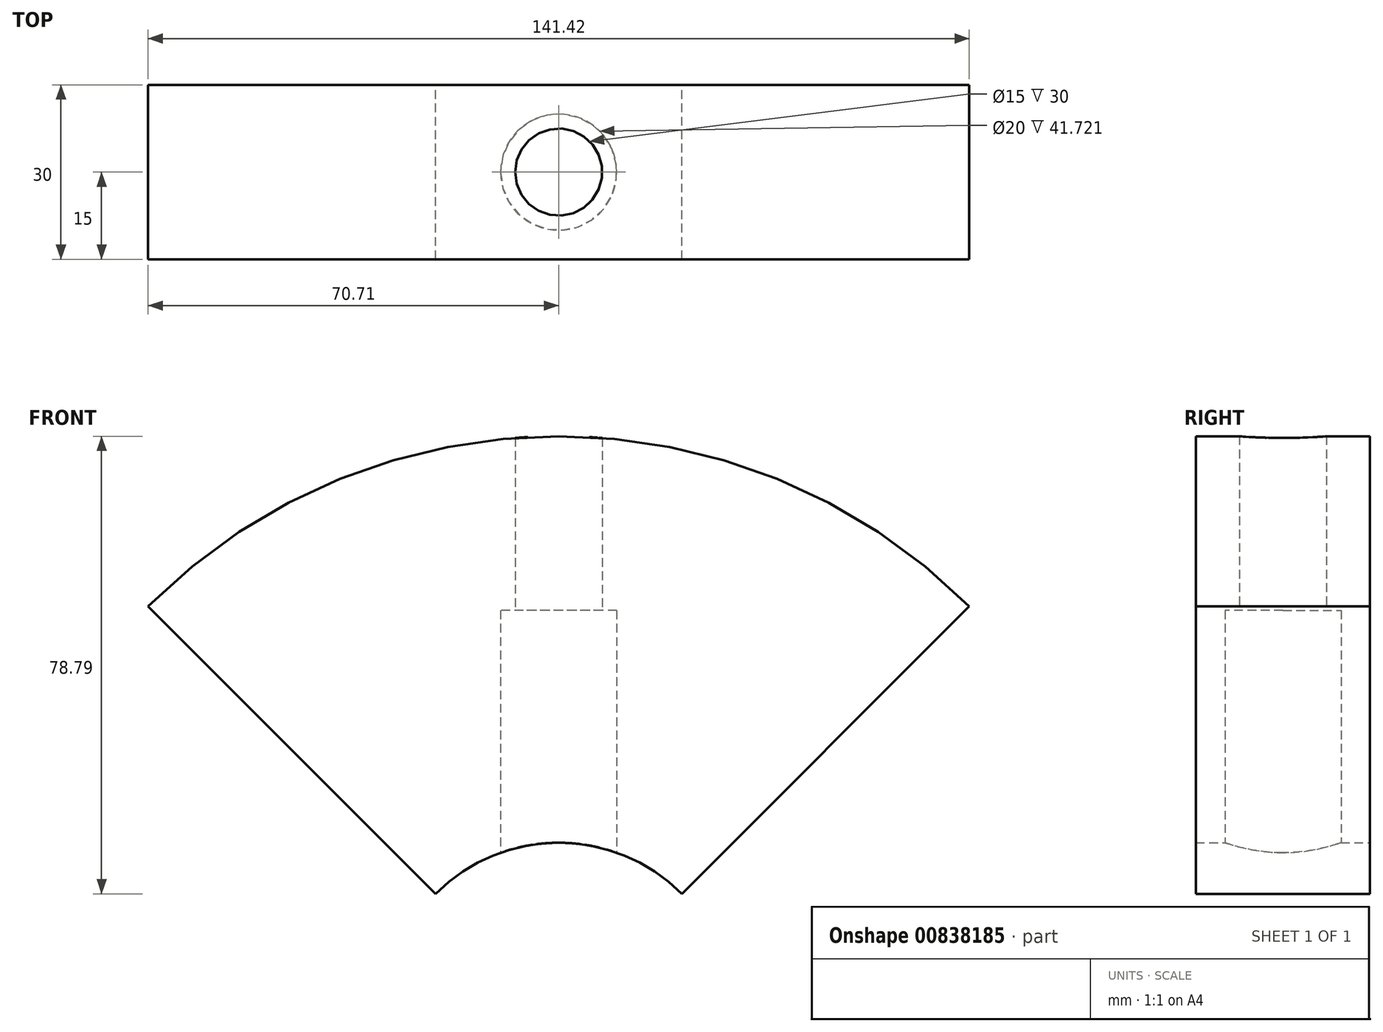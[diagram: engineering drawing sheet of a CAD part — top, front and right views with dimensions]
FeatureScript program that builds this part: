
annotation { "Feature Type Name" : "Feature", "Feature Type Description" : "" }
export const myFeature = defineFeature(function(context is Context, id is Id, definition is map)
    precondition{}
    {
        {
            var Q0;
            Q0=qCreatedBy(makeId("Front.planeOp"),FACE);
            var sketch = newSketch(context, id + "F0", { "sketchPlane" : qUnion([Q0])});
            skArc(sketch, "E0", {"start": v(21.21, 21.21) * mm, "mid": v(0, 30) * mm, "end": v(-21.21, 21.21) * mm});
            skArc(sketch, "E1", {"start": v(70.71, 70.71) * mm, "mid": v(0, 100) * mm, "end": v(-70.71, 70.71) * mm});
            skLineSegment(sketch, "E2.1.0", {"start": v(-70.71, 70.71) * mm, "end": v(-21.21, 21.21) * mm});
            skLineSegment(sketch, "E2.7.0", {"start": v(70.71, 70.71) * mm, "end": v(21.21, 21.21) * mm});
            skPoint(sketch, "E3.orphan", {"position": v(100, 0) * mm});
            skPoint(sketch, "E4.orphan", {"position": v(0, 100) * mm});
            skPoint(sketch, "E5.orphan", {"position": v(-100, 0) * mm});
            skPoint(sketch, "E6.orphan", {"position": v(70.71, -70.71) * mm});
            skLineSegment(sketch, "E7.trimOffspring", {"start": v(-21.21, 21.21) * mm, "end": v(-70.71, 70.71) * mm});
            skLineSegment(sketch, "E8.trimOffspring", {"start": v(21.21, 21.21) * mm, "end": v(70.71, 70.71) * mm});
            skSolve(sketch);
        }
        {
            var Q0;
            Q0 = qSketchRegion(id + "F0", true);
            extrude(context, id + "F1", {"entities" : qUnion([Q0]), "endBound" : BoundingType.SYMMETRIC, "depth" : 30 * mm, "offsetDistance" : 25.4 * mm});
        }
        {
            var Q0;
            Q0=qCreatedBy(makeId("Top.planeOp"),FACE);
            var sketch = newSketch(context, id + "F2", { "sketchPlane" : qUnion([Q0])});
            skCircle(sketch, "E9", {"center": v(0, 0) * mm, "radius": 7.5 * mm});
            skSolve(sketch);
        }
        {
            var Q0;
            Q0 = qSketchRegion(id + "F2", true);
            extrude(context, id + "F3", {"entities" : qUnion([Q0]), "operationType" : NewBodyOperationType.REMOVE, "depth" : 200.66 * mm, "offsetDistance" : 25 * mm});
        }
        {
            var Q0;
            Q0=qCreatedBy(makeId("Top.planeOp"),FACE);
            var sketch = newSketch(context, id + "F4", { "sketchPlane" : qUnion([Q0])});
            skCircle(sketch, "E10", {"center": v(0, 0) * mm, "radius": 10 * mm});
            skSolve(sketch);
        }
        {
            var Q0;
            Q0=makeQuery(id+"F4.imprint","IMPRINT",FACE,{"disambiguationData":[TD([[makeQuery(id+"F4.imprint","IMPRINT",EDGE,{"derivedFrom":sQuery(id+"F4.wireOp",EDGE,"E10")}),1.0]])]});
            extrude(context, id + "F5", {"entities" : qUnion([Q0]), "operationType" : NewBodyOperationType.REMOVE, "depth" : 70 * mm, "offsetDistance" : 25 * mm});
        }
    });
